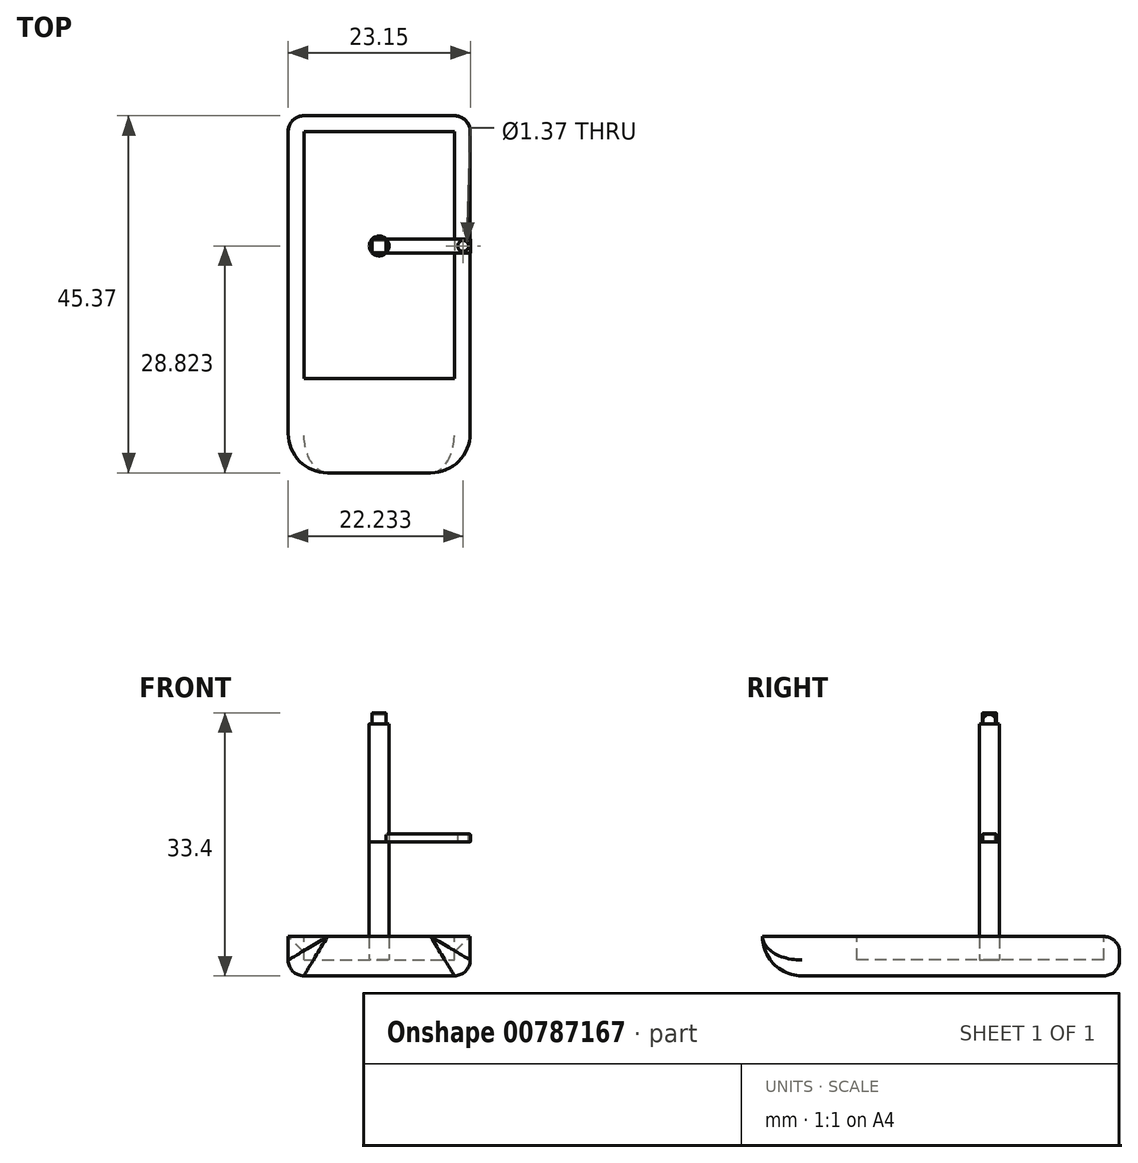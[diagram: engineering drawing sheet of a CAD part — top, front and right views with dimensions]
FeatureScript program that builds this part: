
annotation { "Feature Type Name" : "Feature", "Feature Type Description" : "" }
export const myFeature = defineFeature(function(context is Context, id is Id, definition is map)
    precondition{}
    {
        {
            var Q0;
            Q0=qCreatedBy(makeId("Top.planeOp"),FACE);
            var sketch = newSketch(context, id + "F0", { "sketchPlane" : qUnion([Q0])});
            skLineSegment(sketch, "E0.bottom", {"start": v(-9.24, 8.72) * mm, "end": v(13.88, 8.72) * mm});
            skLineSegment(sketch, "E0.top", {"start": v(-9.24, -26.65) * mm, "end": v(13.88, -26.65) * mm});
            skLineSegment(sketch, "E0.left", {"start": v(-9.24, 8.72) * mm, "end": v(-9.24, -26.65) * mm});
            skLineSegment(sketch, "E0.right", {"start": v(13.88, 8.72) * mm, "end": v(13.88, -26.65) * mm});
            skSolve(sketch);
        }
        {
            var Q0;
            Q0=makeQuery(id+"F0.imprint","IMPRINT",FACE,{"disambiguationData":[TD([[makeQuery(id+"F0.imprint","IMPRINT",EDGE,{"derivedFrom":sQuery(id+"F0.wireOp",EDGE,"E0.bottom")}),-1.0]])]});
            extrude(context, id + "F1", {"entities" : qUnion([Q0]), "depth" : 5 * mm, "offsetDistance" : 25 * mm});
        }
        {
            var Q0;
            Q0=makeQuery(id+"F1.opExtrude","CAP_EDGE",EDGE,{"disambiguationData":[OSD([sQuery(id+"F0.wireOp",EDGE,"E0.bottom")])],"isStart":false});
            var Q1;
            Q1=makeQuery(id+"F1.opExtrude","CAP_EDGE",EDGE,{"disambiguationData":[OSD([sQuery(id+"F0.wireOp",EDGE,"E0.right")])],"isStart":true});
            var Q2;
            Q2=makeQuery(id+"F1.opExtrude","SWEPT_EDGE",EDGE,{"disambiguationData":[OSD([sQuery(id+"F0.wireOp",EDGE,"E0.bottom"),sQuery(id+"F0.wireOp",EDGE,"E0.right")])]});
            var Q3;
            Q3=makeQuery(id+"F1.opExtrude","CAP_EDGE",EDGE,{"disambiguationData":[OSD([sQuery(id+"F0.wireOp",EDGE,"E0.bottom")])],"isStart":true});
            var Q4;
            Q4=makeQuery(id+"F1.opExtrude","SWEPT_EDGE",EDGE,{"disambiguationData":[OSD([sQuery(id+"F0.wireOp",EDGE,"E0.bottom"),sQuery(id+"F0.wireOp",EDGE,"E0.left")])]});
            var Q5;
            Q5=makeQuery(id+"F1.opExtrude","CAP_EDGE",EDGE,{"disambiguationData":[OSD([sQuery(id+"F0.wireOp",EDGE,"E0.left")])],"isStart":true});
            fillet(context, id + "F2", {"entities" : qUnion([Q0, Q1, Q2, Q3, Q4, Q5]), "radius" : 2 * mm, "tangentPropagation" : true, "allowEdgeOverflow" : false});
        }
        {
            var Q0;
            Q0=makeQuery(id+"F1.opExtrude","CAP_FACE",FACE,{"disambiguationData":[OSD([sQuery(id+"F0.wireOp",EDGE,"E0.bottom"),sQuery(id+"F0.wireOp",EDGE,"E0.top"),sQuery(id+"F0.wireOp",EDGE,"E0.left"),sQuery(id+"F0.wireOp",EDGE,"E0.right")])],"isStart":false});
            var sketch = newSketch(context, id + "F3", { "sketchPlane" : qUnion([Q0])});
            skLineSegment(sketch, "E1.bottom", {"start": v(-7.24, 6.72) * mm, "end": v(11.88, 6.72) * mm});
            skLineSegment(sketch, "E1.top", {"start": v(-7.24, -24.65) * mm, "end": v(11.88, -24.65) * mm});
            skLineSegment(sketch, "E1.left", {"start": v(-7.24, 6.72) * mm, "end": v(-7.24, -24.65) * mm});
            skLineSegment(sketch, "E1.right", {"start": v(11.88, 6.72) * mm, "end": v(11.88, -24.65) * mm});
            skSolve(sketch);
        }
        {
            var Q0;
            Q0=makeQuery(id+"F3.imprint","IMPRINT",FACE,{"disambiguationData":[TD([[makeQuery(id+"F3.imprint","IMPRINT",EDGE,{"derivedFrom":sQuery(id+"F3.wireOp",EDGE,"E1.bottom")}),1.0]])]});
            extrude(context, id + "F4", {"entities" : qUnion([Q0]), "operationType" : NewBodyOperationType.REMOVE, "oppositeDirection" : true, "depth" : 3 * mm, "offsetDistance" : 25 * mm});
        }
        {
            var Q0;
            Q0=makeQuery(id+"F4.boolean.opBoolean","COPY",FACE,{"derivedFrom":makeQuery(id+"F4.opExtrude","CAP_FACE",FACE,{"disambiguationData":[OSD([sQuery(id+"F3.wireOp",EDGE,"E1.bottom"),sQuery(id+"F3.wireOp",EDGE,"E1.top"),sQuery(id+"F3.wireOp",EDGE,"E1.left"),sQuery(id+"F3.wireOp",EDGE,"E1.right")])],"isStart":false})});
            var sketch = newSketch(context, id + "F5", { "sketchPlane" : qUnion([Q0])});
            skCircle(sketch, "E2", {"center": v(2.32, -7.84) * mm, "radius": 1.26 * mm});
            skPoint(sketch, "E2.centerSnap0", {"position": v(2.32, 6.72) * mm});
            skSolve(sketch);
        }
        {
            var Q0;
            Q0=makeQuery(id+"F5.imprint","IMPRINT",FACE,{"disambiguationData":[TD([[makeQuery(id+"F5.imprint","IMPRINT",EDGE,{"derivedFrom":sQuery(id+"F5.wireOp",EDGE,"E2")}),1.0]])]});
            extrude(context, id + "F6", {"entities" : qUnion([Q0]), "operationType" : NewBodyOperationType.ADD, "depth" : 15 * mm, "offsetDistance" : 25 * mm});
        }
        {
            var Q0;
            Q0=makeQuery(id+"F6.opExtrude","CAP_FACE",FACE,{"disambiguationData":[OSD([sQuery(id+"F5.wireOp",EDGE,"E2")])],"isStart":false});
            var sketch = newSketch(context, id + "F7", { "sketchPlane" : qUnion([Q0])});
            skLineSegment(sketch, "E3.bottom", {"start": v(1.45, -6.93) * mm, "end": v(13.9, -6.93) * mm});
            skLineSegment(sketch, "E3.top", {"start": v(1.45, -8.72) * mm, "end": v(13.9, -8.72) * mm});
            skLineSegment(sketch, "E3.left", {"start": v(1.45, -6.93) * mm, "end": v(1.45, -8.72) * mm});
            skLineSegment(sketch, "E3.right", {"start": v(13.9, -6.93) * mm, "end": v(13.9, -8.72) * mm});
            skSolve(sketch);
        }
        {
            var Q0;
            {var subQ0=sQuery(id+"F7.wireOp",EDGE,"E3.right");Q0=makeQuery(id+"F7.imprint","IMPRINT",FACE,{"disambiguationData":[TD([[makeQuery(id+"F7.imprint","IMPRINT",EDGE,{"derivedFrom":subQ0}),-1.0]])]});}
            extrude(context, id + "F8", {"entities" : qUnion([Q0]), "operationType" : NewBodyOperationType.ADD, "depth" : 1 * mm, "offsetDistance" : 25 * mm});
        }
        {
            var Q0;
            Q0=makeQuery(id+"F6.opExtrude","CAP_FACE",FACE,{"disambiguationData":[OSD([sQuery(id+"F5.wireOp",EDGE,"E2")])],"isStart":false});
            extrude(context, id + "F9", {"entities" : qUnion([Q0]), "depth" : 15 * mm, "offsetDistance" : 25 * mm});
        }
        {
            var Q0;
            Q0=makeQuery(id+"F8.opExtrude","CAP_FACE",FACE,{"disambiguationData":[OSD([sQuery(id+"F5.wireOp",EDGE,"E2"),sQuery(id+"F7.wireOp",EDGE,"E3.bottom"),sQuery(id+"F7.wireOp",EDGE,"E3.top"),sQuery(id+"F7.wireOp",EDGE,"E3.right")])],"isStart":false});
            var sketch = newSketch(context, id + "F10", { "sketchPlane" : qUnion([Q0])});
            skLineSegment(sketch, "E4.bottom", {"start": v(13.9, -6.93) * mm, "end": v(12.08, -6.93) * mm});
            skLineSegment(sketch, "E4.top", {"start": v(13.9, -8.72) * mm, "end": v(12.08, -8.72) * mm});
            skLineSegment(sketch, "E4.left", {"start": v(13.9, -6.93) * mm, "end": v(13.9, -8.72) * mm});
            skLineSegment(sketch, "E4.right", {"start": v(12.08, -6.93) * mm, "end": v(12.08, -8.72) * mm});
            skCircle(sketch, "E5", {"center": v(13, -7.83) * mm, "radius": 0.69 * mm});
            skPoint(sketch, "E5.centerSnap0", {"position": v(13.9, -7.83) * mm});
            skPoint(sketch, "E5.centerSnap1", {"position": v(13, -8.72) * mm});
            skSolve(sketch);
        }
        {
            var Q0;
            Q0=makeQuery(id+"F10.imprint","IMPRINT",FACE,{"disambiguationData":[TD([[makeQuery(id+"F10.imprint","IMPRINT",EDGE,{"derivedFrom":sQuery(id+"F10.wireOp",EDGE,"E5")}),1.0]])]});
            extrude(context, id + "F11", {"entities" : qUnion([Q0]), "operationType" : NewBodyOperationType.REMOVE, "oppositeDirection" : true, "depth" : 1 * mm, "offsetDistance" : 25 * mm});
        }
        {
            var Q0;
            Q0=makeQuery(id+"F8.opExtrude","CAP_EDGE",EDGE,{"disambiguationData":[OSD([sQuery(id+"F7.wireOp",EDGE,"E3.top")])],"isStart":false});
            var Q1;
            Q1=makeQuery(id+"F8.opExtrude","CAP_EDGE",EDGE,{"disambiguationData":[OSD([sQuery(id+"F7.wireOp",EDGE,"E3.bottom")])],"isStart":false});
            var Q2;
            Q2=makeQuery(id+"F8.opExtrude","CAP_EDGE",EDGE,{"disambiguationData":[OSD([sQuery(id+"F7.wireOp",EDGE,"E3.right")])],"isStart":false});
            var Q3;
            Q3=makeQuery(id+"F8.opExtrude","CAP_EDGE",EDGE,{"disambiguationData":[OSD([sQuery(id+"F7.wireOp",EDGE,"E3.right")])],"isStart":true});
            var Q4;
            Q4=makeQuery(id+"F8.opExtrude","CAP_EDGE",EDGE,{"disambiguationData":[OSD([sQuery(id+"F7.wireOp",EDGE,"E3.top")])],"isStart":true});
            var Q5;
            Q5=makeQuery(id+"F8.opExtrude","CAP_EDGE",EDGE,{"disambiguationData":[OSD([sQuery(id+"F7.wireOp",EDGE,"E3.bottom")])],"isStart":true});
            fillet(context, id + "F12", {"entities" : qUnion([Q0, Q1, Q2, Q3, Q4, Q5]), "radius" : 0.1 * mm, "tangentPropagation" : true, "allowEdgeOverflow" : false});
        }
        {
            var Q0;
            Q0=makeQuery(id+"F1.opExtrude","SWEPT_FACE",FACE,{"disambiguationData":[OSD([sQuery(id+"F0.wireOp",EDGE,"E0.top")])]});
            var sketch = newSketch(context, id + "F13", { "sketchPlane" : qUnion([Q0])});
            skLineSegment(sketch, "E6.bottom", {"start": v(-9.24, 5) * mm, "end": v(13.88, 5) * mm});
            skLineSegment(sketch, "E6.top", {"start": v(-9.24, 2) * mm, "end": v(13.88, 2) * mm});
            skLineSegment(sketch, "E6.left", {"start": v(-9.24, 5) * mm, "end": v(-9.24, 2) * mm});
            skLineSegment(sketch, "E6.right", {"start": v(13.88, 5) * mm, "end": v(13.88, 2) * mm});
            skSolve(sketch);
        }
        {
            var Q0;
            Q0=makeQuery(id+"F13.imprint","IMPRINT",FACE,{"disambiguationData":[TD([[makeQuery(id+"F13.imprint","IMPRINT",EDGE,{"derivedFrom":sQuery(id+"F13.wireOp",EDGE,"E6.top")}),-1.0]])]});
            var Q1;
            Q1=makeQuery(id+"F13.imprint","IMPRINT",FACE,{"disambiguationData":[TD([[makeQuery(id+"F13.imprint","IMPRINT",EDGE,{"derivedFrom":sQuery(id+"F13.wireOp",EDGE,"E6.bottom")}),-1.0]])]});
            extrude(context, id + "F14", {"entities" : qUnion([Q0, Q1]), "operationType" : NewBodyOperationType.ADD, "depth" : 10 * mm, "offsetDistance" : 25 * mm});
        }
        {
            var Q0;
            Q0=makeQuery(id+"F14.opExtrude","CAP_EDGE",EDGE,{"disambiguationData":[OSD([sQuery(id+"F0.wireOp",EDGE,"E0.top")])],"isStart":false});
            var Q1;
            Q1=makeQuery(id+"F14.opExtrude","CAP_EDGE",EDGE,{"disambiguationData":[OSD([sQuery(id+"F13.wireOp",EDGE,"E6.right")])],"isStart":false});
            var Q2;
            Q2=makeQuery(id+"F14.opExtrude","CAP_EDGE",EDGE,{"disambiguationData":[OSD([sQuery(id+"F0.wireOp",EDGE,"E0.top"),sQuery(id+"F0.wireOp",EDGE,"E0.right")])],"isStart":false});
            var Q3;
            Q3=makeQuery(id+"F14.opExtrude","CAP_EDGE",EDGE,{"disambiguationData":[OSD([sQuery(id+"F0.wireOp",EDGE,"E0.top"),sQuery(id+"F0.wireOp",EDGE,"E0.left")])],"isStart":false});
            var Q4;
            Q4=makeQuery(id+"F14.opExtrude","CAP_EDGE",EDGE,{"disambiguationData":[OSD([sQuery(id+"F13.wireOp",EDGE,"E6.left")])],"isStart":false});
            fillet(context, id + "F15", {"entities" : qUnion([Q0, Q1, Q2, Q3, Q4]), "radius" : 5 * mm, "tangentPropagation" : true, "allowEdgeOverflow" : false});
        }
        {
            var Q0;
            Q0=makeQuery(id+"F9.opExtrude","CAP_FACE",FACE,{"disambiguationData":[OSD([sQuery(id+"F5.wireOp",EDGE,"E2")])],"isStart":false});
            var sketch = newSketch(context, id + "F16", { "sketchPlane" : qUnion([Q0])});
            skLineSegment(sketch, "E7.bottom", {"start": v(3.2, -6.93) * mm, "end": v(1.43, -6.93) * mm});
            skLineSegment(sketch, "E7.top", {"start": v(3.2, -8.72) * mm, "end": v(1.43, -8.72) * mm});
            skLineSegment(sketch, "E7.left", {"start": v(3.2, -6.93) * mm, "end": v(3.2, -8.72) * mm});
            skLineSegment(sketch, "E7.right", {"start": v(1.43, -6.93) * mm, "end": v(1.43, -8.72) * mm});
            skSolve(sketch);
        }
        {
            var Q0;
            {var subQ1=sQuery(id+"F16.wireOp",EDGE,"E7.top");Q0=makeQuery(id+"F16.imprint","IMPRINT",FACE,{"disambiguationData":[TD([[makeQuery(id+"F16.imprint","IMPRINT",EDGE,{"derivedFrom":subQ1}),-1.0]])]});}
            extrude(context, id + "F17", {"entities" : qUnion([Q0]), "operationType" : NewBodyOperationType.ADD, "depth" : 1.4 * mm, "offsetDistance" : 25 * mm});
        }
        {
            var Q0;
            Q0=makeQuery(id+"F17.opExtrude","SWEPT_FACE",FACE,{"disambiguationData":[OSD([sQuery(id+"F16.wireOp",EDGE,"E7.left")])]});
            var sketch = newSketch(context, id + "F18", { "sketchPlane" : qUnion([Q0])});
            skArc(sketch, "E8", {"start": v(-7.13, 32) * mm, "mid": v(-7.84, 33.2) * mm, "end": v(-8.55, 32) * mm});
            skSolve(sketch);
        }
        {
            var Q0;
            {var subQ0=sQuery(id+"F18.wireOp",EDGE,"E8");Q0=makeQuery(id+"F18.imprint","IMPRINT",FACE,{"disambiguationData":[TD([[makeQuery(id+"F18.imprint","IMPRINT",EDGE,{"derivedFrom":subQ0}),1.0]])]});}
            extrude(context, id + "F19", {"entities" : qUnion([Q0]), "operationType" : NewBodyOperationType.REMOVE, "oppositeDirection" : true, "depth" : 1.8 * mm, "offsetDistance" : 25 * mm});
        }
        {
            var Q0;
            Q0=makeQuery(id+"F17.opExtrude","CAP_EDGE",EDGE,{"disambiguationData":[OSD([sQuery(id+"F16.wireOp",EDGE,"E7.top")])],"isStart":false});
            var Q1;
            Q1=makeQuery(id+"F17.opExtrude","CAP_EDGE",EDGE,{"disambiguationData":[OSD([sQuery(id+"F16.wireOp",EDGE,"E7.left")])],"isStart":false});
            var Q2;
            Q2=makeQuery(id+"F17.opExtrude","CAP_EDGE",EDGE,{"disambiguationData":[OSD([sQuery(id+"F16.wireOp",EDGE,"E7.bottom")])],"isStart":false});
            var Q3;
            Q3=makeQuery(id+"F17.opExtrude","CAP_EDGE",EDGE,{"disambiguationData":[OSD([sQuery(id+"F16.wireOp",EDGE,"E7.right")])],"isStart":false});
            var Q4;
            Q4=makeQuery(id+"F17.opExtrude","SWEPT_EDGE",EDGE,{"disambiguationData":[OSD([sQuery(id+"F16.wireOp",EDGE,"E7.top"),sQuery(id+"F16.wireOp",EDGE,"E7.left")])]});
            var Q5;
            Q5=makeQuery(id+"F17.opExtrude","SWEPT_EDGE",EDGE,{"disambiguationData":[OSD([sQuery(id+"F5.wireOp",EDGE,"E2"),sQuery(id+"F16.wireOp",EDGE,"E7.bottom"),sQuery(id+"F16.wireOp",EDGE,"E7.left")])]});
            var Q6;
            Q6=makeQuery(id+"F17.opExtrude","SWEPT_EDGE",EDGE,{"disambiguationData":[OSD([sQuery(id+"F5.wireOp",EDGE,"E2"),sQuery(id+"F16.wireOp",EDGE,"E7.bottom")])]});
            var Q7;
            Q7=makeQuery(id+"F17.opExtrude","SWEPT_EDGE",EDGE,{"disambiguationData":[OSD([sQuery(id+"F5.wireOp",EDGE,"E2"),sQuery(id+"F16.wireOp",EDGE,"E7.top"),sQuery(id+"F16.wireOp",EDGE,"E7.right")])]});
            fillet(context, id + "F20", {"entities" : qUnion([Q0, Q1, Q2, Q3, Q4, Q5, Q6, Q7]), "radius" : 0.05 * mm, "tangentPropagation" : true, "allowEdgeOverflow" : false});
        }
    });
